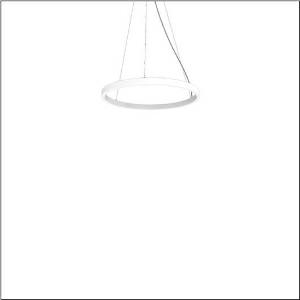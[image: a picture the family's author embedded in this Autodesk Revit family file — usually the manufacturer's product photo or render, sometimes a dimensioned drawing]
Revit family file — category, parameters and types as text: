
# Revit family: silica_r__21_ring-o_5pjbo1d1004a_fa3a
name_source: partatom
category: Lighting Fixtures
units: mm (PartAtom-declared; Revit-internal decimal feet)

## family parameters
Cut with Voids When Loaded = No
Host = Face
Light Source = No
Part Type = Normal
Room Calculation Point = No
Round Connector Dimension = Use Diameter
Shared = No

## types (1)
- Silica® 21 Ring-O (1 x LED, 3740 lm, 60 W, 3000K)
    Apparent Load = 60 VA
    CIE Flux Codes = 2 16 49 50 100
    Color Rendering = 80
    Color Temperature = 3000K
    Default Elevation = 1800 mm
    Description = Silica® 21 Ring-O, suspended luminaire, of PMMA, frosted, light emission: outer ring side luminous distribution, primary light characteristic: symmetric, installation type: suspended mounting, LED, rated luminous flux: 3.744lm, luminous efficacy: 62lm/W, light colour: 830, colour temperature: 3000K, control gear: DALI 2, with terminal, 5-pole, mains connection: 230V, AC/DC, 0/50..60Hz, rated input power: 60W, housing, of extruded aluminium section, traffic white (RAL 9016), diameter: 610mm, ceiling canopy, traffic white (RAL 9016), protection rating (lamp compartment): IP40, insulation class (complete): insulation class I (protective earthing), certification: CE, impact resistance: IK02, permissible operating ambient temperature: 0..+35°C, packaging unit: 1 piece
    Height = 48 mm  [stored 0.15748 ft]
    Lamp = 1 x LED
    Lamp Light Flux = 3740 lm
    Lamp Power = 60 W
    Lamp count = 1
    Length = 610 mm
    Luminous efficacy = 62 lm/W
    Manufacturer = Siteco
    ModVariant = No
    Model = 5PJBO1D1004A
    Mounting Place = Ceiling
    Mounting Type = Pendant
    Number of Poles = 1
    OnlyDefault = Yes
    Power Factor = 1
    Product Name = Silica® 21 Ring-O
    Product group = suspended luminaire
    ProductGroupID = 905
    Protection Class = Protection class I
    Protection Degree = IP 40
    RLX_Detail_Level = 1
    RLX_Emergency_Light_Flux = 0 lm
    RLX_Emergency_Type = 0
    RLX_Emergency_Type_DB = No
    RlxData = <blob elided: 10609 chars, md5=d63fdadb>
    Socket = socket
    Standby Power = 0 W
    System Light Flux = 3740 lm
    System Power = 60 W
    Type Comments = Product without accessories
    Type Image = l_1258379.jpg
    URL = http://relux.com
    VarID = ---
    Voltage = 0 V
    Weight = 0.00 kg
    Width = 0 mm  [stored 0 ft]

note: [stored X ft] marks values corroborated as IEEE doubles in the binary element streams (Revit-internal decimal feet)

## geometry (parser evidence)
native form markers: Sweep x11
no freeform markers — native parametric forms only
